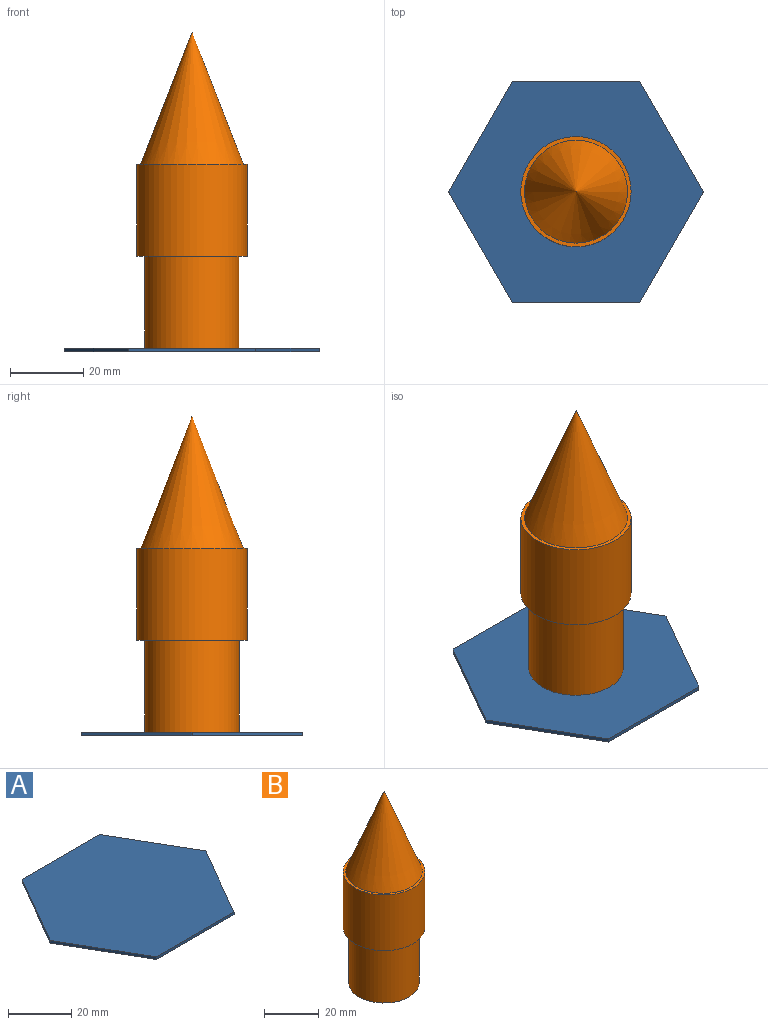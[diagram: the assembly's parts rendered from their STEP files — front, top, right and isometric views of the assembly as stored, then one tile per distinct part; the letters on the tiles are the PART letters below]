
ASSEMBLY  parts=2 mates=2
PART A: 8 faces, bbox 69.3x60x1 mm
  f0: plane 30x17.32mm, normal (-0.87,-0.5,0), area 34.6mm2, adj f1,f5,f6,f7
  f1: plane 34.64x1mm, normal (0,-1,0), area 34.6mm2, adj f0,f2,f6,f7
  f2: plane 30x17.32mm, normal (0.87,-0.5,0), area 34.6mm2, adj f1,f3,f6,f7
  f3: plane 30x17.32mm, normal (0.87,0.5,0), area 34.6mm2, adj f2,f4,f6,f7
  f4: plane 34.64x1mm, normal (0,1,0), area 34.6mm2, adj f3,f5,f6,f7
  f5: plane 30x17.32mm, normal (-0.87,0.5,0), area 34.6mm2, adj f0,f4,f6,f7
  f6: plane 69.28x60mm, normal (0,0,1), area 3117.7mm2, adj f0,f1,f2,f3,f4,f5
  f7: plane 69.28x60mm, normal (0,0,-1), area 3117.7mm2, adj f0,f1,f2,f3,f4,f5
PART B: 10 faces, bbox 30x30x86 mm
  f0: cylinder r=15mm len=30mm, axis (0,0,-1), area 2356.2mm2, adj f1,f2
  f1: plane 30x30mm, normal (0,0,1), area 91.1mm2, adj f0,f3
  f2: plane 30x30mm, normal (0,0,-1), area 188.9mm2, adj f0,f5
  f3: cone r=14mm half-angle=21.3deg, axis (0,0,-1), area 1698.9mm2, adj f1
  f4: cylinder r=11.71mm len=25mm, axis (0,0,1), area 1839.3mm2, adj f6,f9
  f5: cylinder r=12.84mm len=25.68mm, axis (0,0,1), area 2016.9mm2, adj f2,f6
  f6: plane 25.68x25.68mm, normal (0,0,-1), area 87.2mm2, adj f4,f5
  f7: plane 19.21x19.21mm, normal (0,0,-1), area 289.9mm2, adj f8
  f8: cylinder r=9.61mm len=19.21mm, axis (0,0,-1), area 603.5mm2, adj f7,f9
  f9: plane 23.42x23.42mm, normal (0,0,-1), area 140.9mm2, adj f4,f8
PLACE A t=(23.81,-67.29,-48.13)mm
PLACE B t=(23.81,-67.29,-22.13)mm
MATE cylindrical B.f5 <-> A.f6  axis (0,0,1) through (23.81,-67.29,-34.63)mm
MATE planar B.f5 <-> A.f6  axis (0,0,-1) through (23.81,-67.29,-47.13)mm
